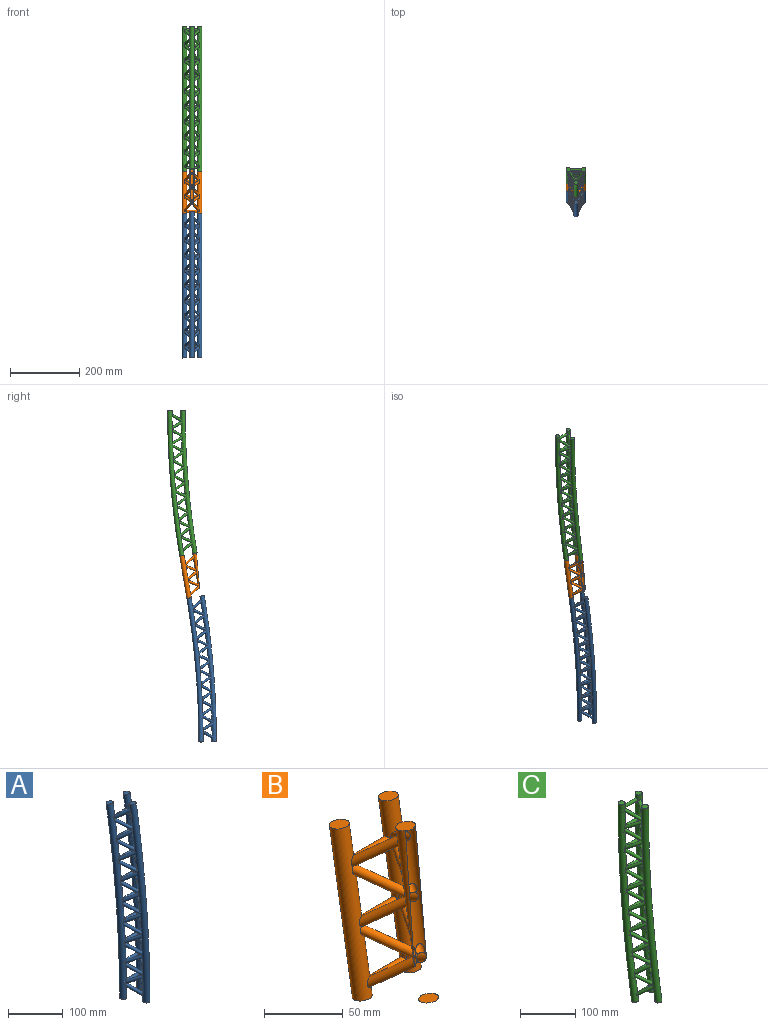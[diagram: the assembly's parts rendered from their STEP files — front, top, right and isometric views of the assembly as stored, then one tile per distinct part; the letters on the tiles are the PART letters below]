
ASSEMBLY  parts=3 mates=6
PART A: 54 faces, bbox 56.7x94.2x425.9 mm
  f0: plane 12.7x12.7mm, normal (0,0,-1), area 126.7mm2, adj f2
  f1: plane 12.7x12.53mm, normal (0,0.17,0.99), area 126.7mm2, adj f2
  f2: torus R=2527.3mm, axis (-1,0,0), area 15774.9mm2, adj f0,f1,f3,f4,f5,f6,f7,f8
  f3: cylinder r=3.17mm len=31.44mm, axis (-0.45,-0.7,0.55), area 715.5mm2, adj f2,f4,f19,f53
  f4: cylinder r=3.17mm len=35.17mm, axis (-0.45,-0.83,-0.34), area 715.3mm2, adj f2,f3,f19,f30
  f5: bspline ~44.21x13.02mm, area 645.7mm2, adj f2,f11
  f6: cylinder r=3.17mm len=32.04mm, axis (-0.45,-0.72,0.53), area 715.5mm2, adj f2,f7,f19,f31
  f7: cylinder r=3.17mm len=34.81mm, axis (-0.45,-0.81,-0.37), area 715.3mm2, adj f2,f6,f19,f42
  f8: bspline ~44.21x12.81mm, area 645.7mm2, adj f2,f11
  f9: plane 12.7x12.7mm, normal (0,0,-1), area 126.7mm2, adj f11
  f10: plane 12.7x12.53mm, normal (0,0.17,0.99), area 126.7mm2, adj f11
  f11: torus R=2527.3mm, axis (-1,0,0), area 15798.4mm2, adj f5,f8,f9,f10,f14,f15,f16,f22
  f12: cylinder r=3.17mm len=33.13mm, axis (-0.45,-0.76,0.47), area 715.4mm2, adj f2,f13,f19,f48
  f13: cylinder r=3.17mm len=33.98mm, axis (-0.45,-0.79,-0.43), area 715.3mm2, adj f2,f12,f19,f20
  f14: cylinder r=3.17mm len=33.13mm, axis (0.45,-0.76,0.47), area 715.5mm2, adj f11,f15,f19,f45
  f15: cylinder r=3.17mm len=33.97mm, axis (0.45,-0.79,-0.43), area 715.3mm2, adj f11,f14,f19,f22
  f16: bspline ~44.21x13.02mm, area 645.7mm2, adj f2,f11
  f17: plane 12.7x12.7mm, normal (0,0,-1), area 126.7mm2, adj f19
  f18: plane 12.7x12.53mm, normal (0,0.17,0.99), area 126.7mm2, adj f19
  f19: torus R=2565.4mm, axis (-1,0,0), area 15669mm2, adj f3,f4,f6,f7,f12,f13,f14,f15
  f20: cylinder r=3.17mm len=33.38mm, axis (-0.45,-0.77,0.46), area 715.5mm2, adj f2,f13,f19,f21
  f21: cylinder r=3.17mm len=33.74mm, axis (-0.45,-0.78,-0.44), area 714.9mm2, adj f2,f19,f20
  f22: cylinder r=3.17mm len=33.38mm, axis (0.45,-0.77,0.46), area 715.5mm2, adj f11,f15,f19,f23
  f23: cylinder r=3.17mm len=33.74mm, axis (0.45,-0.78,-0.44), area 716.9mm2, adj f11,f19,f22
  f24: bspline ~44.21x13.11mm, area 645.7mm2, adj f2,f11
  f25: cylinder r=3.17mm len=32.6mm, axis (-0.45,-0.74,0.5), area 715.5mm2, adj f2,f19,f26,f43
  f26: cylinder r=3.17mm len=34.41mm, axis (-0.45,-0.8,-0.4), area 715.3mm2, adj f2,f19,f25,f47
  f27: cylinder r=3.17mm len=32.6mm, axis (0.45,-0.74,0.5), area 715.5mm2, adj f11,f19,f28,f40
  f28: cylinder r=3.17mm len=34.41mm, axis (0.45,-0.8,-0.4), area 715.3mm2, adj f11,f19,f27,f46
  f29: bspline ~44.21x12.81mm, area 645.7mm2, adj f2,f11
  f30: cylinder r=3.17mm len=31.74mm, axis (-0.45,-0.71,0.54), area 715.5mm2, adj f2,f4,f19,f31
  f31: cylinder r=3.17mm len=34.99mm, axis (-0.45,-0.82,-0.36), area 715.3mm2, adj f2,f6,f19,f30
  f32: cylinder r=3.17mm len=31.74mm, axis (0.45,-0.71,0.54), area 715.5mm2, adj f11,f19,f33,f37
  f33: cylinder r=3.17mm len=35mm, axis (0.45,-0.82,-0.36), area 715.3mm2, adj f11,f19,f32,f36
  f34: bspline ~44.21x12.91mm, area 645.7mm2, adj f2,f11
  f35: cylinder r=3.17mm len=34.8mm, axis (0.45,-0.81,-0.37), area 715.3mm2, adj f11,f19,f36,f41
  f36: cylinder r=3.17mm len=32.04mm, axis (0.45,-0.72,0.53), area 715.5mm2, adj f11,f19,f33,f35
  f37: cylinder r=3.17mm len=35.17mm, axis (0.45,-0.83,-0.34), area 715.3mm2, adj f11,f19,f32,f38
  f38: cylinder r=3.17mm len=31.44mm, axis (0.45,-0.7,0.55), area 715.5mm2, adj f11,f19,f37,f50
  f39: bspline ~44.21x12.7mm, area 645.7mm2, adj f2,f11
  f40: cylinder r=3.17mm len=34.61mm, axis (0.45,-0.81,-0.39), area 715.3mm2, adj f11,f19,f27,f41
  f41: cylinder r=3.17mm len=32.32mm, axis (0.45,-0.73,0.51), area 715.5mm2, adj f11,f19,f35,f40
  f42: cylinder r=3.17mm len=32.32mm, axis (-0.45,-0.73,0.51), area 715.5mm2, adj f2,f7,f19,f43
  f43: cylinder r=3.17mm len=34.61mm, axis (-0.45,-0.81,-0.39), area 715.3mm2, adj f2,f19,f25,f42
  f44: bspline ~44.21x12.91mm, area 645.7mm2, adj f2,f11
  f45: cylinder r=3.17mm len=34.19mm, axis (0.45,-0.79,-0.41), area 715.3mm2, adj f11,f14,f19,f46
  f46: cylinder r=3.17mm len=32.87mm, axis (0.45,-0.75,0.49), area 715.5mm2, adj f11,f19,f28,f45
  f47: cylinder r=3.17mm len=32.87mm, axis (-0.45,-0.75,0.49), area 715.5mm2, adj f2,f19,f26,f48
  f48: cylinder r=3.17mm len=34.2mm, axis (-0.45,-0.79,-0.41), area 715.3mm2, adj f2,f12,f19,f47
  f49: bspline ~44.21x13.11mm, area 645.7mm2, adj f2,f11
  f50: cylinder r=3.17mm len=35.34mm, axis (0.45,-0.83,-0.33), area 715.3mm2, adj f11,f19,f38,f51
  f51: cylinder r=3.17mm len=31.13mm, axis (0.45,-0.69,0.56), area 717.1mm2, adj f11,f19,f50
  f52: cylinder r=3.17mm len=31.13mm, axis (-0.45,-0.69,0.56), area 717mm2, adj f2,f19,f53
  f53: cylinder r=3.17mm len=35.34mm, axis (-0.45,-0.83,-0.33), area 715.3mm2, adj f2,f3,f19,f52
PART B: 25 faces, bbox 82.1x96.2x157.3 mm
  f0: cylinder r=6.35mm len=5.46mm, axis (0,-0.17,-0.99), area 5.3mm2, adj f1,f2,f3,f4
  f1: cylinder r=3.17mm len=35.46mm, axis (-0.45,0.84,0.31), area 712.9mm2, adj f0,f4,f5,f6,f7
  f2: cylinder r=3.17mm len=35.46mm, axis (0.45,0.84,0.31), area 712.9mm2, adj f0,f3,f6,f8,f9
  f3: cylinder r=3.17mm len=30.95mm, axis (0.45,0.69,-0.57), area 714.8mm2, adj f0,f2,f6,f8
  f4: cylinder r=3.17mm len=30.95mm, axis (-0.45,0.69,-0.57), area 714.7mm2, adj f0,f1,f5,f6
  f5: cylinder r=6.35mm len=125.61mm, axis (0,-0.17,-0.99), area 4718.3mm2, adj f1,f4,f7,f10,f11,f12,f13,f14
  f6: cylinder r=6.35mm len=103.03mm, axis (0,-0.17,-0.99), area 3554.1mm2, adj f1,f2,f3,f4,f7,f9,f14,f15
  f7: cylinder r=3.17mm len=30.95mm, axis (-0.45,0.69,-0.57), area 712.9mm2, adj f1,f5,f6,f14,f20
  f8: cylinder r=6.35mm len=125.61mm, axis (0,-0.17,-0.99), area 4718.3mm2, adj f2,f3,f9,f12,f13,f16,f17,f18
  f9: cylinder r=3.17mm len=30.95mm, axis (0.45,0.69,-0.57), area 712.9mm2, adj f2,f6,f8,f17,f20
  f10: plane 12.7x12.53mm, normal (0,-0.17,-0.99), area 126.7mm2, adj f5
  f11: plane 12.7x12.53mm, normal (0,0.17,0.99), area 126.7mm2, adj f5
  f12: cylinder r=3.17mm len=33mm, axis (1,0,0), area 640.9mm2, adj f5,f8
  f13: cylinder r=3.17mm len=33mm, axis (1,0,0), area 640.9mm2, adj f5,f8
  f14: cylinder r=3.17mm len=35.46mm, axis (-0.45,0.84,0.31), area 712.9mm2, adj f5,f6,f7,f15,f20
  f15: cylinder r=3.17mm len=30.95mm, axis (-0.45,0.69,-0.57), area 714.7mm2, adj f5,f6,f14
  f16: cylinder r=3.17mm len=33mm, axis (1,0,0), area 641mm2, adj f5,f8
  f17: cylinder r=3.17mm len=35.46mm, axis (0.45,0.84,0.31), area 712.9mm2, adj f6,f8,f9,f18,f20
  f18: cylinder r=3.17mm len=30.95mm, axis (0.45,0.69,-0.57), area 714.7mm2, adj f6,f8,f17
  f19: plane 12.7x12.53mm, normal (0,0.17,0.99), area 126.7mm2, adj f6
  f20: cylinder r=6.35mm len=5.46mm, axis (0,-0.17,-0.99), area 5.3mm2, adj f7,f9,f14,f17
  f21: plane 12.7x12.53mm, normal (0,-0.17,-0.99), area 126.7mm2, adj f8
  f22: plane 12.7x12.53mm, normal (0,0.17,0.99), area 126.7mm2, adj f8
  f23: cylinder r=6.35mm len=12.53mm, axis (0,-0.17,-0.99), area 0mm2, adj f24
  f24: plane 38.1x37.93mm, normal (0,-0.17,-0.99), area 126.7mm2, adj f23
PART C: 55 faces, bbox 56.7x94x423.8 mm
  f0: plane 12.7x12.7mm, normal (0,0,1), area 126.7mm2, adj f2
  f1: plane 12.7x12.53mm, normal (0,-0.17,-0.99), area 126.7mm2, adj f2
  f2: torus R=2552.7mm, axis (-1,0,0), area 15904.1mm2, adj f0,f1,f9,f10,f11,f12,f13,f14
  f3: plane 12.7x12.7mm, normal (0,0,1), area 126.7mm2, adj f5
  f4: plane 12.7x12.53mm, normal (0,-0.17,-0.99), area 126.7mm2, adj f5
  f5: torus R=2514.6mm, axis (-1,0,0), area 15345.4mm2, adj f3,f4,f10,f11,f13,f15,f16,f17
  f6: plane 12.7x12.7mm, normal (0,0,1), area 126.7mm2, adj f8
  f7: plane 12.7x12.53mm, normal (0,-0.17,-0.99), area 126.7mm2, adj f8
  f8: torus R=2552.7mm, axis (-1,0,0), area 15905.3mm2, adj f6,f7,f9,f12,f14,f16,f17,f18
  f9: cylinder r=3.17mm len=33.11mm, axis (-1,0,0), area 641mm2, adj f2,f8
  f10: cylinder r=3.17mm len=32.57mm, axis (0.45,0.74,-0.5), area 713.4mm2, adj f2,f5,f41,f43
  f11: cylinder r=3.17mm len=34.14mm, axis (0.45,0.79,0.41), area 713.3mm2, adj f2,f5,f13,f15
  f12: cylinder r=3.17mm len=33.11mm, axis (-1,0,0), area 641mm2, adj f2,f8
  f13: cylinder r=3.17mm len=32.83mm, axis (0.45,0.75,-0.48), area 713.4mm2, adj f2,f5,f11,f41
  f14: cylinder r=3.17mm len=33.11mm, axis (-1,0,0), area 641mm2, adj f2,f8
  f15: cylinder r=3.17mm len=33.09mm, axis (0.45,0.76,-0.47), area 713.4mm2, adj f2,f5,f11,f21
  f16: cylinder r=3.17mm len=32.83mm, axis (-0.45,0.75,-0.48), area 713.4mm2, adj f5,f8,f19,f20
  f17: cylinder r=3.17mm len=33.09mm, axis (-0.45,0.76,-0.47), area 713.4mm2, adj f5,f8,f18,f19
  f18: cylinder r=3.17mm len=33.92mm, axis (-0.45,0.79,0.42), area 713.4mm2, adj f5,f8,f17,f53
  f19: cylinder r=3.17mm len=34.14mm, axis (-0.45,0.79,0.41), area 713.4mm2, adj f5,f8,f16,f17
  f20: cylinder r=3.17mm len=34.35mm, axis (-0.45,0.8,0.4), area 713.4mm2, adj f5,f8,f16,f39
  f21: cylinder r=3.17mm len=33.92mm, axis (0.45,0.79,0.42), area 713.3mm2, adj f2,f5,f15,f37
  f22: cylinder r=3.17mm len=33.11mm, axis (-1,0,0), area 641mm2, adj f2,f8
  f23: cylinder r=3.17mm len=32.29mm, axis (-0.45,0.73,-0.51), area 713.3mm2, adj f5,f8,f25,f26
  f24: cylinder r=3.17mm len=33.11mm, axis (-1,0,0), area 641mm2, adj f2,f8
  f25: cylinder r=3.17mm len=34.74mm, axis (-0.45,0.81,0.37), area 713.4mm2, adj f5,f8,f23,f54
  f26: cylinder r=3.17mm len=34.55mm, axis (-0.45,0.81,0.38), area 713.4mm2, adj f5,f8,f23,f39
  f27: cylinder r=3.17mm len=32.29mm, axis (0.45,0.73,-0.51), area 713.3mm2, adj f2,f5,f43,f51
  f28: cylinder r=3.17mm len=35.27mm, axis (0.45,0.83,0.33), area 713.3mm2, adj f2,f5,f40,f42
  f29: cylinder r=3.17mm len=35.27mm, axis (-0.45,0.83,0.33), area 713.4mm2, adj f5,f8,f47,f48
  f30: cylinder r=3.17mm len=33.11mm, axis (-1,0,0), area 641.1mm2, adj f2,f8
  f31: cylinder r=3.17mm len=33.11mm, axis (-1,0,0), area 641.1mm2, adj f2,f8
  f32: cylinder r=3.17mm len=33.69mm, axis (-0.45,0.78,0.44), area 713.8mm2, adj f5,f8,f53
  f33: cylinder r=3.17mm len=33.11mm, axis (-1,0,0), area 641mm2, adj f2,f8
  f34: cylinder r=3.17mm len=33.11mm, axis (-1,0,0), area 641.1mm2, adj f2,f8
  f35: cylinder r=3.17mm len=34.92mm, axis (-0.45,0.82,0.35), area 713.4mm2, adj f5,f8,f45,f54
  f36: cylinder r=3.17mm len=35.1mm, axis (-0.45,0.83,0.34), area 713.4mm2, adj f5,f8,f45,f48
  f37: cylinder r=3.17mm len=33.34mm, axis (0.45,0.77,-0.46), area 713.4mm2, adj f2,f5,f21,f38
  f38: cylinder r=3.17mm len=33.69mm, axis (0.45,0.78,0.44), area 713.9mm2, adj f2,f5,f37
  f39: cylinder r=3.17mm len=32.57mm, axis (-0.45,0.74,-0.5), area 713.4mm2, adj f5,f8,f20,f26
  f40: cylinder r=3.17mm len=31.11mm, axis (0.45,0.7,-0.56), area 713.8mm2, adj f2,f5,f28
  f41: cylinder r=3.17mm len=34.35mm, axis (0.45,0.8,0.4), area 713.4mm2, adj f2,f5,f10,f13
  f42: cylinder r=3.17mm len=31.42mm, axis (0.45,0.71,-0.55), area 713.4mm2, adj f2,f5,f28,f50
  f43: cylinder r=3.17mm len=34.55mm, axis (0.45,0.81,0.38), area 713.4mm2, adj f2,f5,f10,f27
  f44: cylinder r=3.17mm len=32.01mm, axis (0.45,0.72,-0.52), area 713.3mm2, adj f2,f5,f49,f51
  f45: cylinder r=3.17mm len=31.72mm, axis (-0.45,0.72,-0.54), area 713.4mm2, adj f5,f8,f35,f36
  f46: cylinder r=3.17mm len=31.72mm, axis (0.45,0.72,-0.54), area 713.4mm2, adj f2,f5,f49,f50
  f47: cylinder r=3.17mm len=31.11mm, axis (-0.45,0.7,-0.56), area 713.8mm2, adj f5,f8,f29
  f48: cylinder r=3.17mm len=31.42mm, axis (-0.45,0.71,-0.55), area 713.4mm2, adj f5,f8,f29,f36
  f49: cylinder r=3.17mm len=34.92mm, axis (0.45,0.82,0.35), area 713.4mm2, adj f2,f5,f44,f46
  f50: cylinder r=3.17mm len=35.1mm, axis (0.45,0.83,0.34), area 713.3mm2, adj f2,f5,f42,f46
  f51: cylinder r=3.17mm len=34.74mm, axis (0.45,0.81,0.37), area 713.4mm2, adj f2,f5,f27,f44
  f52: cylinder r=3.17mm len=33.11mm, axis (-1,0,0), area 641.1mm2, adj f2,f8
  f53: cylinder r=3.17mm len=33.34mm, axis (-0.45,0.77,-0.46), area 713.4mm2, adj f5,f8,f18,f32
  f54: cylinder r=3.17mm len=32.01mm, axis (-0.45,0.72,-0.52), area 713.4mm2, adj f5,f8,f25,f35
PLACE A t=(-0.73,-55.9,-468.11)mm
PLACE B t=(-0.73,71.1,-468.11)mm
PLACE C t=(-0.73,34.44,493.85)mm
MATE cylindrical C.f4 <-> A.f18  axis (0,-0.17,-0.99) through (-0.73,-25.44,78.82)mm
MATE planar B.f0 <-> C.f4  axis (0,0.17,0.99) through (-0.73,-25.44,78.82)mm
MATE cylindrical B.f0 <-> A.f18  axis (0,-0.17,-0.99) through (-0.73,-46.11,-44.7)mm
MATE cylindrical A.f1 <-> B.f8  axis (0,0.17,0.99) through (21.27,-8.54,-50.98)mm
MATE planar A.f18 <-> B.f0  axis (0,0.17,0.99) through (-0.73,-46.11,-44.7)mm
MATE cylindrical C.f1 <-> A.f1  axis (0,-0.17,-0.99) through (21.27,12.13,72.53)mm
